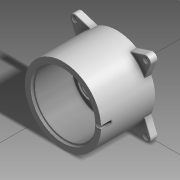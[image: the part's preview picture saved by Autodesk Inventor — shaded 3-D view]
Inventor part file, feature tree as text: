
AUTODESK INVENTOR PART (.ipt)
format: ipt  version: 2013 (Build 170138000, 138)  size: 623,616 bytes
history: native  units: in
note: dims shown in document units (in); Inventor stores cm internally (conversion verified against a paired STEP export)
features: extrude x17, sketch x17, reference x4, fillet x1
ambient origin geometry x8: Origin, YZ Plane, XZ Plane, XY Plane, X Axis, Y Axis, Z Axis, Center Point
bodies: Solid1 (feature_tree)
feature tree (39):
  extrude  "Extrusion1"  Depth=0.1969in TaperAngle=0.0deg
  extrude  "Extrusion14"  Depth=1.3953in TaperAngle=0.0deg
  extrude  "Extrusion15"  Depth=0.6339in
  extrude  "Extrusion39"  Depth=0.0394in
  extrude  "Extrusion17"  Depth=0.315in TaperAngle=0.0deg
  extrude  "Extrusion18"  Depth=0.2756in TaperAngle=0.0deg
  extrude  "Extrusion19"  Depth=0.2362in TaperAngle=0.0deg
  extrude  "Extrusion20"  Depth=0.1969in TaperAngle=0.0deg
  extrude  "Extrusion21"  Depth=0.1575in TaperAngle=0.0deg
  extrude  "Extrusion22"  Depth=0.1181in TaperAngle=0.0deg
  extrude  "Extrusion23"  Depth=0.0787in TaperAngle=0.0deg
  extrude  "Extrusion24"  Depth=0.0394in TaperAngle=0.0deg
  extrude  "Extrusion25"  Depth=0.9843in
  extrude  "Extrusion38"  Depth=0.1102in
  sketch  "Sketch40"  dims[d137=0.0394in d138=0.0394in d139=0.0in]
  extrude  "Extrusion40"  Depth=2.3622in
  extrude  "Extrusion41"  Depth=1.1002in
  extrude  "Extrusion42"  Depth=2.2in
  fillet  "Fillet1"  Radius=0.1575in
  sketch  "Sketch1"  dims[d9=0.1969in d10=0.0in]
  reference  "Reference2"
  reference  "Reference3"
  reference  "Reference4"
  reference  "Reference5"
  sketch  "Sketch15"  dims[d11=0.1181in d12=0.1181in d35=0.3937in d36=0.5906in d37=0.7874in d38=0.9843in d39=0.3937in d40=0.5906in d41=1.1811in d42=1.378in d43=1.5748in d44=1.7717in d94=0.1969in d95=0.0in]
  sketch  "Sketch17"  dims[d96=1.811in d100=1.3953in d101=0.0in]
  sketch  "Sketch18"  dims[d111=0.8189in d112=0.6339in]
  sketch  "Sketch19"  dims[d113=0.4331in d114=0.0in d115=0.0394in]
  sketch  "Sketch20"  dims[d116=0.0394in d117=0.315in d118=0.0in]
  sketch  "Sketch21"  dims[d119=0.0394in d120=0.2756in d121=0.0in]
  sketch  "Sketch22"  dims[d122=0.0394in d123=0.2362in d124=0.0in]
  sketch  "Sketch23"  dims[d125=0.0394in d126=0.1969in d127=0.0in]
  sketch  "Sketch24"  dims[d128=0.0394in d129=0.1575in d130=0.0in]
  sketch  "Sketch25"  dims[d131=0.0394in d132=0.1181in d133=0.0in]
  sketch  "Sketch39"  dims[d134=0.0394in d135=0.0787in d136=0.0in]
  sketch  "Sketch41"  dims[d217=0.9843in d219=0.9843in]
  sketch  "Sketch42"  dims[d220=0.063in d221=0.0in d222=0.1102in]
  sketch  "Sketch43"  dims[d223=0.2756in d231=2.3622in]
  sketch  "Sketch44"  dims[d233=1.5748in d234=1.1002in d264=2.2in d287=0.1575in d288=0.0787in d289=0.0in d291=2.1in d292=1.95in d293=0.1102in d294=0.1102in d295=1.0651in d296=1.0651in d297=2.2441in d298=1.2179in d299=1.122in d300=1.0651in d301=0.1378in d302=1.0651in d303=1.122in d304=0.1575in d305=0.1575in d306=1.811in d307=2.2441in d308=1.811in d310=1.9055in d311=0.0787in d312=0.0in d313=0.2992in d314=0.0in d315=0.1181in d317=1.0236in d318=0.1181in d319=0.0866in d320=0.1575in d321=0.0512in d323=0.1181in d324=0.0in d325=0.0197in]
